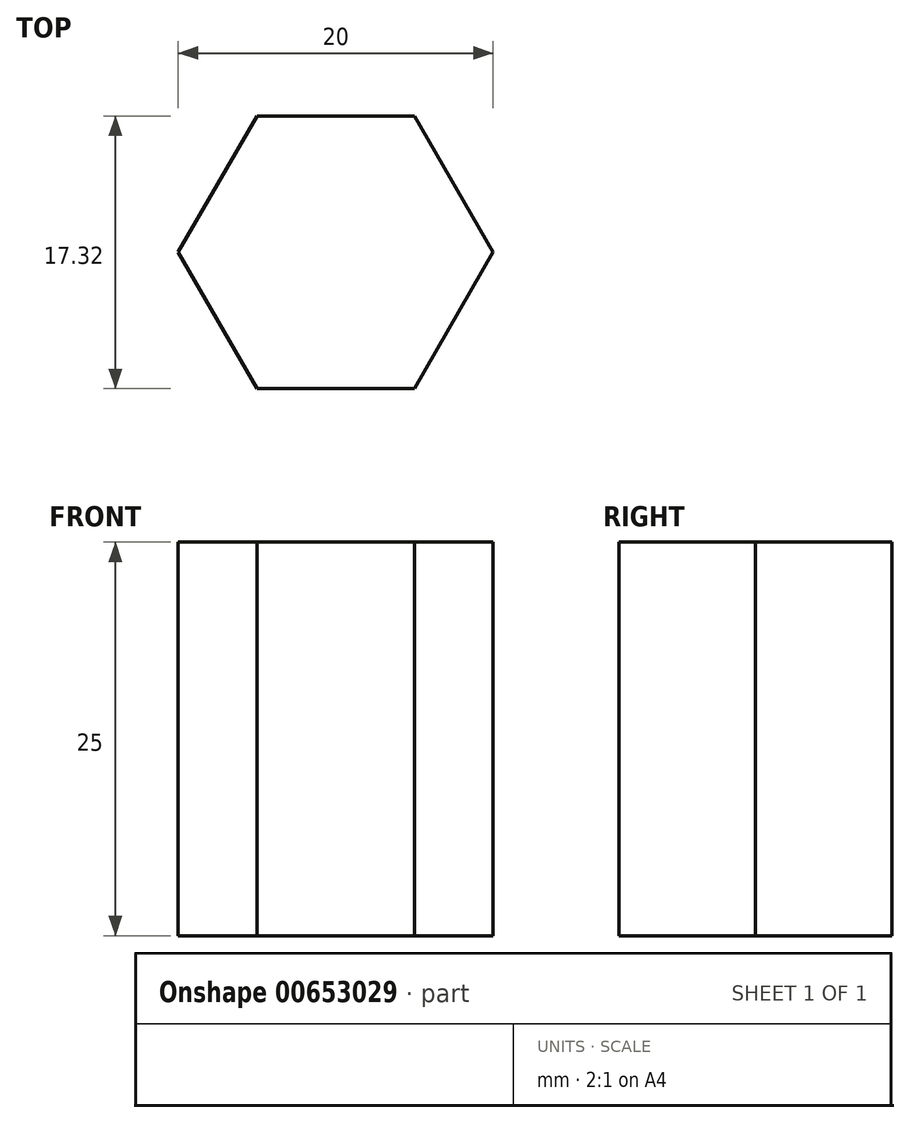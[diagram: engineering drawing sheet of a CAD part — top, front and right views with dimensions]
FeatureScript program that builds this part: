
annotation { "Feature Type Name" : "Feature", "Feature Type Description" : "" }
export const myFeature = defineFeature(function(context is Context, id is Id, definition is map)
    precondition{}
    {
        {
            var Q0;
            Q0=qCreatedBy(makeId("Top.planeOp"),FACE);
            var sketch = newSketch(context, id + "F0", { "sketchPlane" : qUnion([Q0])});
            skCircle(sketch, "E0.cCircle", {"center": v(0, 0) * mm, "radius": 8.66 * mm, "construction": true});
            skLineSegment(sketch, "E0.0", {"start": v(-5, 8.66) * mm, "end": v(5, 8.66) * mm});
            skLineSegment(sketch, "E0.1", {"start": v(5, 8.66) * mm, "end": v(10, 0) * mm});
            skLineSegment(sketch, "E0.2", {"start": v(10, 0) * mm, "end": v(5, -8.66) * mm});
            skLineSegment(sketch, "E0.3", {"start": v(5, -8.66) * mm, "end": v(-5, -8.66) * mm});
            skLineSegment(sketch, "E0.4", {"start": v(-5, -8.66) * mm, "end": v(-10, 0) * mm});
            skLineSegment(sketch, "E0.5", {"start": v(-10, 0) * mm, "end": v(-5, 8.66) * mm});
            skPoint(sketch, "E0.0.midPoint", {"position": v(0, 8.66) * mm});
            skSolve(sketch);
        }
        {
            var Q0;
            Q0=makeQuery(id+"F0.imprint","IMPRINT",FACE,{"disambiguationData":[TD([[makeQuery(id+"F0.imprint","IMPRINT",EDGE,{"derivedFrom":sQuery(id+"F0.wireOp",EDGE,"E0.0")}),-1.0]])]});
            extrude(context, id + "F1", {"entities" : qUnion([Q0]), "depth" : 25 * mm, "offsetDistance" : 25 * mm});
        }
    });
